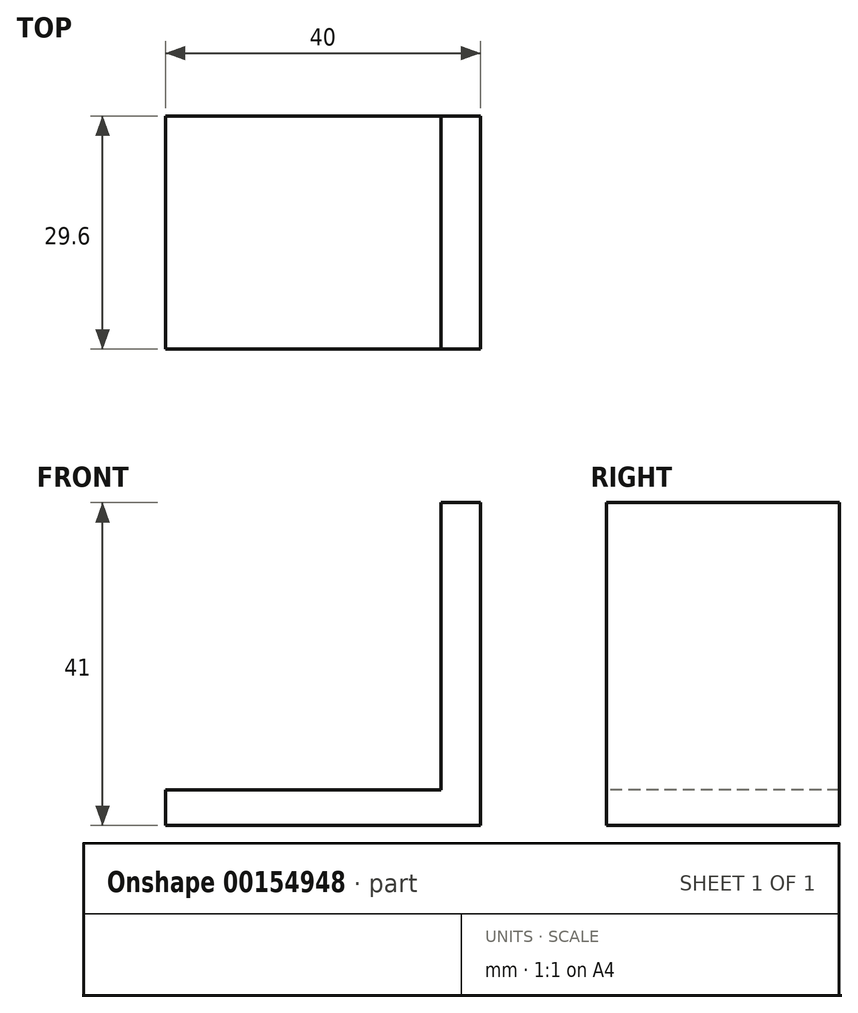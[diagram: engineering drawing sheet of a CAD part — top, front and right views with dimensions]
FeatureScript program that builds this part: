
annotation { "Feature Type Name" : "Feature", "Feature Type Description" : "" }
export const myFeature = defineFeature(function(context is Context, id is Id, definition is map)
    precondition{}
    {
        {
            var Q0;
            Q0=qCreatedBy(makeId("Top.planeOp"),FACE);
            var sketch = newSketch(context, id + "F0", { "sketchPlane" : qUnion([Q0])});
            skLineSegment(sketch, "E0.bottom", {"start": v(-20, -14.8) * mm, "end": v(20, -14.8) * mm});
            skLineSegment(sketch, "E0.top", {"start": v(-20, 14.8) * mm, "end": v(20, 14.8) * mm});
            skLineSegment(sketch, "E0.left", {"start": v(-20, -14.8) * mm, "end": v(-20, 14.8) * mm});
            skLineSegment(sketch, "E0.right", {"start": v(20, -14.8) * mm, "end": v(20, 14.8) * mm});
            skPoint(sketch, "E0.middle", {"position": v(0, 0) * mm});
            skSolve(sketch);
        }
        {
            var Q0;
            Q0 = qSketchRegion(id + "F0", true);
            extrude(context, id + "F1", {"entities" : qUnion([Q0]), "depth" : 41 * mm});
        }
        {
            var Q0;
            Q0=makeQuery(id+"F1.opExtrude","SWEPT_FACE",FACE,{"disambiguationData":[OSD([sQuery(id+"F0.wireOp",EDGE,"E0.bottom")])]});
            var sketch = newSketch(context, id + "F2", { "sketchPlane" : qUnion([Q0])});
            skLineSegment(sketch, "E1.bottom", {"start": v(15, 41) * mm, "end": v(-20, 41) * mm});
            skLineSegment(sketch, "E1.top", {"start": v(15, 4.5) * mm, "end": v(-20, 4.5) * mm});
            skLineSegment(sketch, "E1.left", {"start": v(15, 41) * mm, "end": v(15, 4.5) * mm});
            skLineSegment(sketch, "E1.right", {"start": v(-20, 41) * mm, "end": v(-20, 4.5) * mm});
            skSolve(sketch);
        }
        {
            var Q0;
            Q0 = qSketchRegion(id + "F2", true);
            extrude(context, id + "F3", {"entities" : qUnion([Q0]), "operationType" : NewBodyOperationType.REMOVE, "endBound" : BoundingType.THROUGH_ALL, "oppositeDirection" : true, "depth" : 25 * mm});
        }
    });
